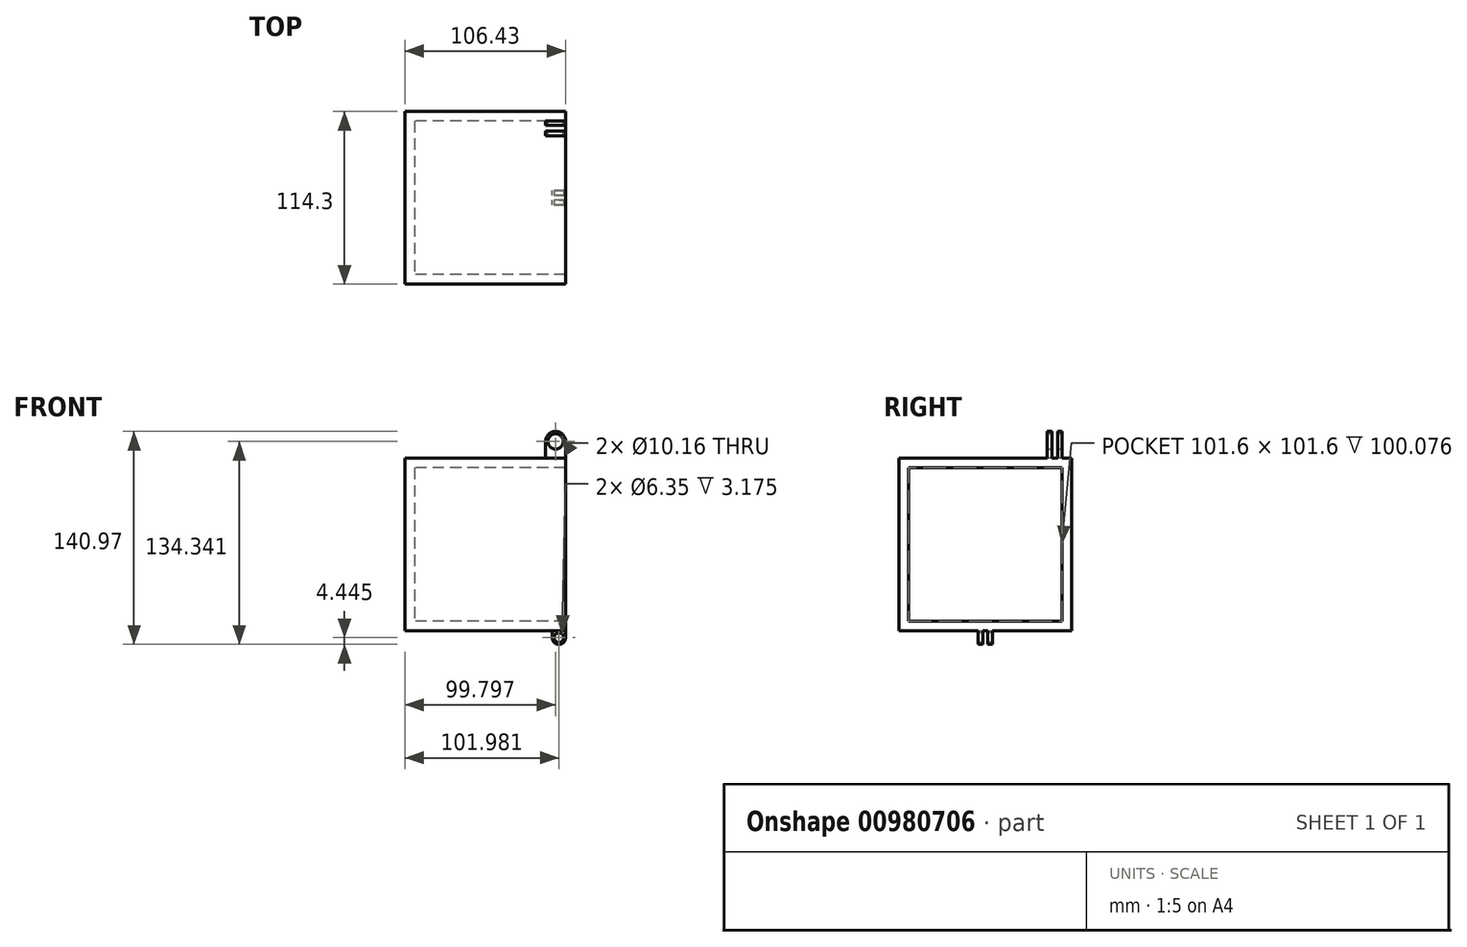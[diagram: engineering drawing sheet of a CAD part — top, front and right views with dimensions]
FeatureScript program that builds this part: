
annotation { "Feature Type Name" : "Feature", "Feature Type Description" : "" }
export const myFeature = defineFeature(function(context is Context, id is Id, definition is map)
    precondition{}
    {
        {
            var Q0;
            Q0=qCreatedBy(makeId("Right.planeOp"),FACE);
            var sketch = newSketch(context, id + "F0", { "sketchPlane" : qUnion([Q0])});
            skLineSegment(sketch, "E0.bottom", {"start": v(57.15, 57.15) * mm, "end": v(-57.15, 57.15) * mm});
            skLineSegment(sketch, "E0.top", {"start": v(57.15, -57.15) * mm, "end": v(-57.15, -57.15) * mm});
            skLineSegment(sketch, "E0.left", {"start": v(57.15, 57.15) * mm, "end": v(57.15, -57.15) * mm});
            skLineSegment(sketch, "E0.right", {"start": v(-57.15, 57.15) * mm, "end": v(-57.15, -57.15) * mm});
            skPoint(sketch, "E0.middle", {"position": v(0, 0) * mm});
            skLineSegment(sketch, "E1.bottom", {"start": v(50.8, 50.8) * mm, "end": v(-50.8, 50.8) * mm});
            skLineSegment(sketch, "E1.top", {"start": v(50.8, -50.8) * mm, "end": v(-50.8, -50.8) * mm});
            skLineSegment(sketch, "E1.left", {"start": v(50.8, 50.8) * mm, "end": v(50.8, -50.8) * mm});
            skLineSegment(sketch, "E1.right", {"start": v(-50.8, 50.8) * mm, "end": v(-50.8, -50.8) * mm});
            skSolve(sketch);
        }
        {
            var Q0;
            Q0=qSketchRegion(id+"F0",true);
            var Q1;
            Q1=makeQuery(id+"F0.imprint","IMPRINT",FACE,{"disambiguationData":[TD([[makeQuery(id+"F0.imprint","IMPRINT",EDGE,{"derivedFrom":sQuery(id+"F0.wireOp",EDGE,"E0.bottom")}),1.0]])]});
            extrude(context, id + "F1", {"entities" : qUnion([Q0, Q1]), "depth" : 106.43 * mm, "offsetDistance" : 25.4 * mm});
        }
        {
            var Q0;
            Q0=qCreatedBy(makeId("Right.planeOp"),FACE);
            var sketch = newSketch(context, id + "F2", { "sketchPlane" : qUnion([Q0])});
            skLineSegment(sketch, "E2.bottom", {"start": v(-57.15, 57.15) * mm, "end": v(57.15, 57.15) * mm});
            skLineSegment(sketch, "E2.top", {"start": v(-57.15, -57.15) * mm, "end": v(57.15, -57.15) * mm});
            skLineSegment(sketch, "E2.left", {"start": v(-57.15, 57.15) * mm, "end": v(-57.15, -57.15) * mm});
            skLineSegment(sketch, "E2.right", {"start": v(57.15, 57.15) * mm, "end": v(57.15, -57.15) * mm});
            skSolve(sketch);
        }
        {
            var Q0;
            Q0=qSketchRegion(id+"F2",true);
            extrude(context, id + "F3", {"entities" : qUnion([Q0]), "operationType" : NewBodyOperationType.ADD, "depth" : 6.35 * mm, "offsetDistance" : 25.4 * mm});
        }
        {
            var Q0;
            Q0=makeQuery(id+"F1.opExtrude","SWEPT_FACE",FACE,{"disambiguationData":[OSD([sQuery(id+"F0.wireOp",EDGE,"E0.bottom")])]});
            var sketch = newSketch(context, id + "F4", { "sketchPlane" : qUnion([Q0])});
            skLineSegment(sketch, "E3.bottom", {"start": v(106.43, 50.8) * mm, "end": v(93.17, 50.8) * mm});
            skLineSegment(sketch, "E3.top", {"start": v(106.43, 41.15) * mm, "end": v(93.17, 41.15) * mm});
            skLineSegment(sketch, "E3.left", {"start": v(106.43, 50.8) * mm, "end": v(106.43, 41.15) * mm});
            skLineSegment(sketch, "E3.right", {"start": v(93.17, 50.8) * mm, "end": v(93.17, 41.15) * mm});
            skSolve(sketch);
        }
        {
            var Q0;
            Q0=makeQuery(id+"F4.imprint","IMPRINT",FACE,{"disambiguationData":[TD([[makeQuery(id+"F4.imprint","IMPRINT",EDGE,{"derivedFrom":sQuery(id+"F4.wireOp",EDGE,"E3.bottom")}),1.0]])]});
            extrude(context, id + "F5", {"entities" : qUnion([Q0]), "operationType" : NewBodyOperationType.ADD, "depth" : 17.78 * mm, "offsetDistance" : 25.4 * mm});
        }
        {
            var Q0;
            Q0=makeQuery(id+"F5.boolean.opBoolean","MERGE",FACE,{"derivedFrom":[makeQuery(id+"F1.opExtrude","CAP_FACE",FACE,{"disambiguationData":[OSD([sQuery(id+"F0.wireOp",EDGE,"E0.bottom"),sQuery(id+"F0.wireOp",EDGE,"E0.top"),sQuery(id+"F0.wireOp",EDGE,"E0.left"),sQuery(id+"F0.wireOp",EDGE,"E0.right"),sQuery(id+"F0.wireOp",EDGE,"E1.bottom"),sQuery(id+"F0.wireOp",EDGE,"E1.top"),sQuery(id+"F0.wireOp",EDGE,"E1.left"),sQuery(id+"F0.wireOp",EDGE,"E1.right")])],"isStart":false}),makeQuery(id+"F5.opExtrude","SWEPT_FACE",FACE,{"disambiguationData":[OSD([sQuery(id+"F4.wireOp",EDGE,"E3.left")])]})]});
            var sketch = newSketch(context, id + "F6", { "sketchPlane" : qUnion([Q0])});
            skLineSegment(sketch, "E4.bottom", {"start": v(47.88, 74.93) * mm, "end": v(44.07, 74.93) * mm});
            skLineSegment(sketch, "E4.top", {"start": v(47.88, 57.15) * mm, "end": v(44.07, 57.15) * mm});
            skLineSegment(sketch, "E4.left", {"start": v(47.88, 74.93) * mm, "end": v(47.88, 57.15) * mm});
            skLineSegment(sketch, "E4.right", {"start": v(44.07, 74.93) * mm, "end": v(44.07, 57.15) * mm});
            skSolve(sketch);
        }
        {
            var Q0;
            Q0=qSketchRegion(id+"F6",true);
            extrude(context, id + "F7", {"entities" : qUnion([Q0]), "operationType" : NewBodyOperationType.REMOVE, "endBound" : BoundingType.THROUGH_ALL, "oppositeDirection" : true, "depth" : 25.4 * mm, "offsetDistance" : 25.4 * mm});
        }
        {
            var Q0;
            {var subQ0=sQuery(id+"F4.wireOp",EDGE,"E3.left");var subQ1=sQuery(id+"F4.wireOp",EDGE,"E3.bottom");Q0=makeQuery(id+"F7.boolean.opBoolean","SPLIT",EDGE,{"disambiguationData":[TD([makeQuery(id+"F5.opExtrude","SWEPT_FACE",FACE,{"disambiguationData":[OSD([subQ1])]})])],"derivedFrom":makeQuery(id+"F5.opExtrude","CAP_EDGE",EDGE,{"disambiguationData":[OSD([subQ0])],"isStart":false})});}
            var Q1;
            {var subQ0=sQuery(id+"F4.wireOp",EDGE,"E3.left");var subQ1=sQuery(id+"F4.wireOp",EDGE,"E3.top");Q1=makeQuery(id+"F7.boolean.opBoolean","SPLIT",EDGE,{"disambiguationData":[TD([makeQuery(id+"F5.opExtrude","SWEPT_FACE",FACE,{"disambiguationData":[OSD([subQ1])]})])],"derivedFrom":makeQuery(id+"F5.opExtrude","CAP_EDGE",EDGE,{"disambiguationData":[OSD([subQ0])],"isStart":false})});}
            var Q2;
            {var subQ0=sQuery(id+"F4.wireOp",EDGE,"E3.bottom");var subQ1=sQuery(id+"F4.wireOp",EDGE,"E3.right");Q2=makeQuery(id+"F7.boolean.opBoolean","SPLIT",EDGE,{"disambiguationData":[TD([makeQuery(id+"F5.opExtrude","SWEPT_FACE",FACE,{"disambiguationData":[OSD([subQ0])]})])],"derivedFrom":makeQuery(id+"F5.opExtrude","CAP_EDGE",EDGE,{"disambiguationData":[OSD([subQ1])],"isStart":false})});}
            var Q3;
            {var subQ0=sQuery(id+"F4.wireOp",EDGE,"E3.right");var subQ1=sQuery(id+"F4.wireOp",EDGE,"E3.top");Q3=makeQuery(id+"F7.boolean.opBoolean","SPLIT",EDGE,{"disambiguationData":[TD([makeQuery(id+"F5.opExtrude","SWEPT_FACE",FACE,{"disambiguationData":[OSD([subQ1])]})])],"derivedFrom":makeQuery(id+"F5.opExtrude","CAP_EDGE",EDGE,{"disambiguationData":[OSD([subQ0])],"isStart":false})});}
            fillet(context, id + "F8", {"entities" : qUnion([Q0, Q1, Q2, Q3]), "radius" : 6.63 * mm, "tangentPropagation" : true, "allowEdgeOverflow" : false});
        }
        {
            var Q0;
            Q0=makeQuery(id+"F5.opExtrude","SWEPT_FACE",FACE,{"disambiguationData":[OSD([sQuery(id+"F4.wireOp",EDGE,"E3.bottom")])]});
            var sketch = newSketch(context, id + "F9", { "sketchPlane" : qUnion([Q0])});
            skCircle(sketch, "E5", {"center": v(-99.8, 68.3) * mm, "radius": 5.08 * mm});
            skSolve(sketch);
        }
        {
            var Q0;
            Q0=qSketchRegion(id+"F9",true);
            extrude(context, id + "F10", {"entities" : qUnion([Q0]), "operationType" : NewBodyOperationType.REMOVE, "oppositeDirection" : true, "depth" : 25.4 * mm, "offsetDistance" : 25.4 * mm});
        }
        {
            var Q0;
            Q0=makeQuery(id+"F1.opExtrude","SWEPT_FACE",FACE,{"disambiguationData":[OSD([sQuery(id+"F0.wireOp",EDGE,"E0.top")])]});
            var sketch = newSketch(context, id + "F11", { "sketchPlane" : qUnion([Q0])});
            skLineSegment(sketch, "E6.bottom", {"start": v(106.43, 4.83) * mm, "end": v(97.54, 4.83) * mm});
            skLineSegment(sketch, "E6.top", {"start": v(106.43, 1.65) * mm, "end": v(97.54, 1.65) * mm});
            skLineSegment(sketch, "E6.left", {"start": v(106.43, 4.83) * mm, "end": v(106.43, 1.65) * mm});
            skLineSegment(sketch, "E6.right", {"start": v(97.54, 4.83) * mm, "end": v(97.54, 1.65) * mm});
            skLineSegment(sketch, "E7.bottom", {"start": v(106.43, -1.65) * mm, "end": v(97.54, -1.65) * mm});
            skLineSegment(sketch, "E7.top", {"start": v(106.43, -4.83) * mm, "end": v(97.54, -4.83) * mm});
            skLineSegment(sketch, "E7.left", {"start": v(106.43, -1.65) * mm, "end": v(106.43, -4.83) * mm});
            skLineSegment(sketch, "E7.right", {"start": v(97.54, -1.65) * mm, "end": v(97.54, -4.83) * mm});
            skLineSegment(sketch, "E8", {"start": v(106.43, 0) * mm, "end": v(106.43, -1.65) * mm, "construction": true});
            skLineSegment(sketch, "E9", {"start": v(106.43, 0) * mm, "end": v(106.43, 1.65) * mm, "construction": true});
            skSolve(sketch);
        }
        {
            var Q0;
            Q0=qSketchRegion(id+"F11",true);
            extrude(context, id + "F12", {"entities" : qUnion([Q0]), "operationType" : NewBodyOperationType.ADD, "depth" : 8.9 * mm, "offsetDistance" : 25.4 * mm});
        }
        {
            var Q0;
            Q0=makeQuery(id+"F12.opExtrude","CAP_EDGE",EDGE,{"disambiguationData":[OSD([sQuery(id+"F11.wireOp",EDGE,"E6.right")])],"isStart":false});
            var Q1;
            Q1=makeQuery(id+"F12.opExtrude","CAP_EDGE",EDGE,{"disambiguationData":[OSD([sQuery(id+"F11.wireOp",EDGE,"E7.right")])],"isStart":false});
            var Q2;
            Q2=makeQuery(id+"F12.opExtrude","CAP_EDGE",EDGE,{"disambiguationData":[OSD([sQuery(id+"F11.wireOp",EDGE,"E7.left")])],"isStart":false});
            var Q3;
            Q3=makeQuery(id+"F12.opExtrude","CAP_EDGE",EDGE,{"disambiguationData":[OSD([sQuery(id+"F11.wireOp",EDGE,"E6.left")])],"isStart":false});
            fillet(context, id + "F13", {"entities" : qUnion([Q0, Q1, Q2, Q3]), "radius" : 4.44 * mm, "tangentPropagation" : true, "allowEdgeOverflow" : false});
        }
        {
            var Q0;
            Q0=makeQuery(id+"F12.opExtrude","SWEPT_FACE",FACE,{"disambiguationData":[OSD([sQuery(id+"F11.wireOp",EDGE,"E6.bottom")])]});
            var sketch = newSketch(context, id + "F14", { "sketchPlane" : qUnion([Q0])});
            skCircle(sketch, "E10", {"center": v(101.98, -61.6) * mm, "radius": 3.17 * mm});
            skSolve(sketch);
        }
        {
            var Q0;
            Q0=qSketchRegion(id+"F14",true);
            extrude(context, id + "F15", {"entities" : qUnion([Q0]), "operationType" : NewBodyOperationType.REMOVE, "oppositeDirection" : true, "depth" : 25.4 * mm, "offsetDistance" : 25.4 * mm});
        }
    });
